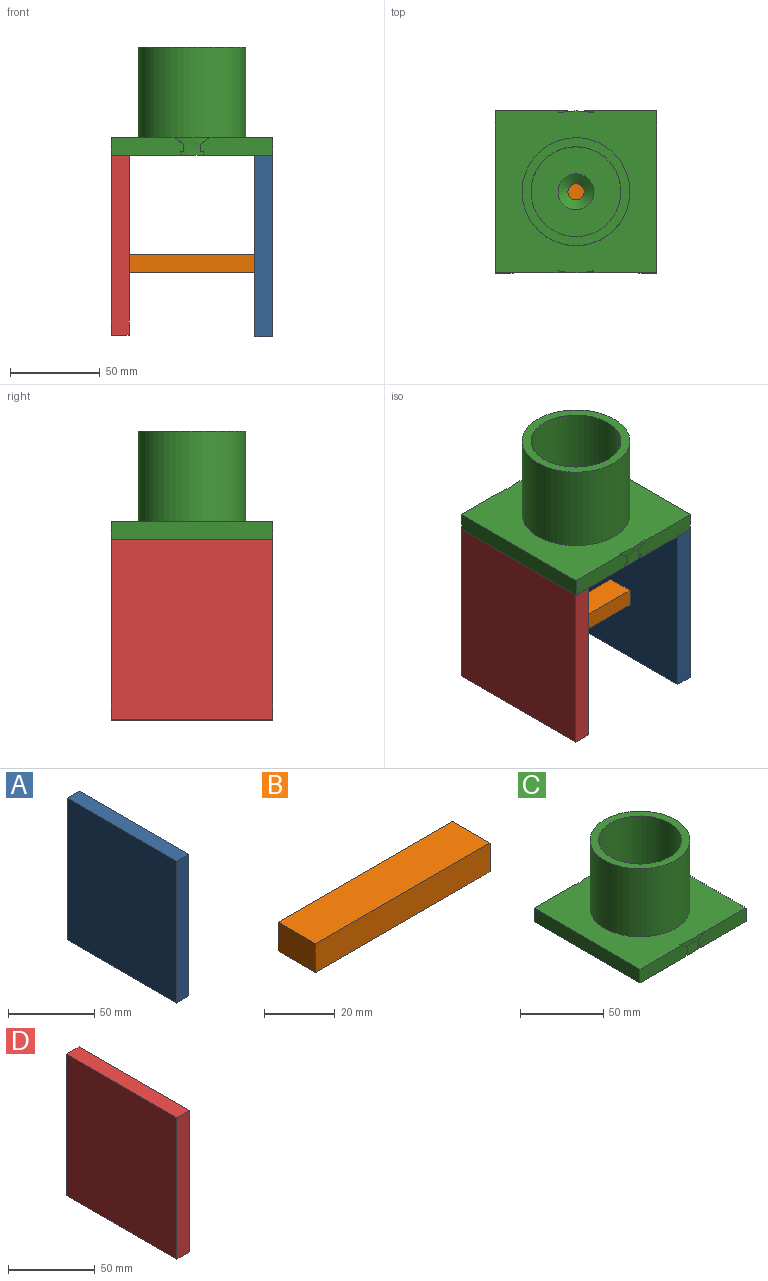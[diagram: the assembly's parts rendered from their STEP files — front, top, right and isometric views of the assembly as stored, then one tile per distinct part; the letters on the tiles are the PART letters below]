
ASSEMBLY  parts=4 mates=3
PART A: 6 faces, bbox 10x90x100.8 mm
  f0: plane 90x10mm, normal (0,0,1), area 900mm2, adj f1,f3,f4,f5
  f1: plane 100.84x90mm, normal (-1,0,0), area 9075.6mm2, adj f0,f2,f4,f5
  f2: plane 90x10mm, normal (0,0,-1), area 900mm2, adj f1,f3,f4,f5
  f3: plane 100.84x90mm, normal (1,0,0), area 9075.6mm2, adj f0,f2,f4,f5
  f4: plane 100.84x10mm, normal (0,-1,0), area 1008.4mm2, adj f0,f1,f2,f3
  f5: plane 100.84x10mm, normal (0,1,0), area 1008.4mm2, adj f0,f1,f2,f3
PART B: 6 faces, bbox 70x15x10 mm
  f0: plane 70x15mm, normal (0,0,1), area 1050mm2, adj f1,f3,f4,f5
  f1: plane 15x10mm, normal (-1,0,0), area 150mm2, adj f0,f2,f4,f5
  f2: plane 70x15mm, normal (0,0,-1), area 1050mm2, adj f1,f3,f4,f5
  f3: plane 15x10mm, normal (1,0,0), area 150mm2, adj f0,f2,f4,f5
  f4: plane 70x10mm, normal (0,-1,0), area 700mm2, adj f0,f1,f2,f3
  f5: plane 70x10mm, normal (0,1,0), area 700mm2, adj f0,f1,f2,f3
PART C: 34 faces, bbox 90x90x60 mm
  f0: cylinder r=45mm len=20mm, axis (0,0,1), area 120.4mm2, adj f3,f4,f15,f18,f19,f20,f26,f27
  f1: cylinder r=45mm len=20mm, axis (0,0,1), area 120.4mm2, adj f3,f4,f13,f14,f16,f17,f24,f25
  f2: cylinder r=30mm len=60mm, axis (0,0,1), area 9424.8mm2, adj f3,f11
  f3: plane 90x90mm, normal (0,0,1), area 5257.6mm2, adj f0,f1,f2,f12,f17,f18,f21,f22
  f4: plane 90x90mm, normal (0,0,-1), area 7963.2mm2, adj f0,f1,f5,f12,f13,f20,f21,f22
  f5: cylinder r=6.5mm len=13mm, axis (0,0,1), area 81.7mm2, adj f4,f6
  f6: plane 13x13mm, normal (0,0,-1), area 69.1mm2, adj f5,f7
  f7: cylinder r=4.5mm len=9mm, axis (0,0,1), area 113.1mm2, adj f6,f8
  f8: cone r=4.5mm half-angle=54deg, axis (0,0,1), area 309.8mm2, adj f7,f9
  f9: plane 50x50mm, normal (0,0,1), area 1649.3mm2, adj f8,f10
  f10: cylinder r=25mm len=50mm, axis (0,0,1), area 7854mm2, adj f9,f11
  f11: plane 60x60mm, normal (0,0,1), area 863.9mm2, adj f2,f10
  f12: plane 90x10mm, normal (-1,0,0), area 900mm2, adj f3,f4,f21,f22
  f13: plane 2x0.47mm, normal (1,0,0), area 0.9mm2, adj f1,f4,f14,f21
  f14: plane 2x0.47mm, normal (0,0,-1), area 0.7mm2, adj f1,f13,f16,f21
  f15: plane 2x0.47mm, normal (0,0,-1), area 0.7mm2, adj f0,f19,f20,f22
  f16: plane 4x0.23mm, normal (1,0,0), area 0.9mm2, adj f1,f14,f17,f21
  f17: plane 5.5x4mm, normal (0.59,0,0.81), area 4.2mm2, adj f1,f3,f16,f21
  f18: plane 5.5x4mm, normal (0.59,0,0.81), area 4.2mm2, adj f0,f3,f19,f22
  f19: plane 4x0.23mm, normal (1,0,0), area 0.9mm2, adj f0,f15,f18,f22
  f20: plane 2x0.47mm, normal (1,0,0), area 0.9mm2, adj f0,f4,f15,f22
  f21: plane 40.5x10mm, normal (0,-1,0), area 390mm2, adj f3,f4,f12,f13,f14,f16,f17
  f22: plane 40.5x10mm, normal (0,1,0), area 390mm2, adj f3,f4,f12,f15,f18,f19,f20
  f23: plane 90x10mm, normal (1,0,0), area 900mm2, adj f3,f4,f32,f33
  f24: plane 2x0.47mm, normal (-1,0,0), area 0.9mm2, adj f1,f4,f25,f32
  f25: plane 2x0.47mm, normal (0,0,-1), area 0.7mm2, adj f1,f24,f30,f32
  f26: plane 2x0.47mm, normal (0,0,-1), area 0.7mm2, adj f0,f27,f31,f33
  f27: plane 4x0.23mm, normal (-1,0,0), area 0.9mm2, adj f0,f26,f29,f33
  f28: plane 5.5x4mm, normal (-0.59,0,0.81), area 4.2mm2, adj f1,f3,f30,f32
  f29: plane 5.5x4mm, normal (-0.59,0,0.81), area 4.2mm2, adj f0,f3,f27,f33
  f30: plane 4x0.23mm, normal (-1,0,0), area 0.9mm2, adj f1,f25,f28,f32
  f31: plane 2x0.47mm, normal (-1,0,0), area 0.9mm2, adj f0,f4,f26,f33
  f32: plane 40.5x10mm, normal (0,-1,0), area 390mm2, adj f3,f4,f23,f24,f25,f28,f30
  f33: plane 40.5x10mm, normal (0,1,0), area 390mm2, adj f3,f4,f23,f26,f27,f29,f31
PART D: 6 faces, bbox 10x90x100 mm
  f0: plane 100x90mm, normal (1,0,0), area 9000mm2, adj f1,f3,f4,f5
  f1: plane 90x10mm, normal (0,0,1), area 900mm2, adj f0,f2,f4,f5
  f2: plane 100x90mm, normal (-1,0,0), area 9000mm2, adj f1,f3,f4,f5
  f3: plane 90x10mm, normal (0,0,-1), area 900mm2, adj f0,f2,f4,f5
  f4: plane 100x10mm, normal (0,-1,0), area 1000mm2, adj f0,f1,f2,f3
  f5: plane 100x10mm, normal (0,1,0), area 1000mm2, adj f0,f1,f2,f3
PLACE A t=(0,0,-43.78)mm
PLACE B t=(0,0,-49.48)mm
PLACE C at identity fixed
PLACE D t=(0,0,-44.06)mm
MATE fastened D.f1 <-> C.f4  axis (0,0,1) through (-40,0,-10)mm
MATE fastened B.f3 <-> A.f1  axis (1,0,0) through (35,0,-70.42)mm
MATE fastened A.f0 <-> C.f4  axis (0,0,1) through (40,0,-10)mm
